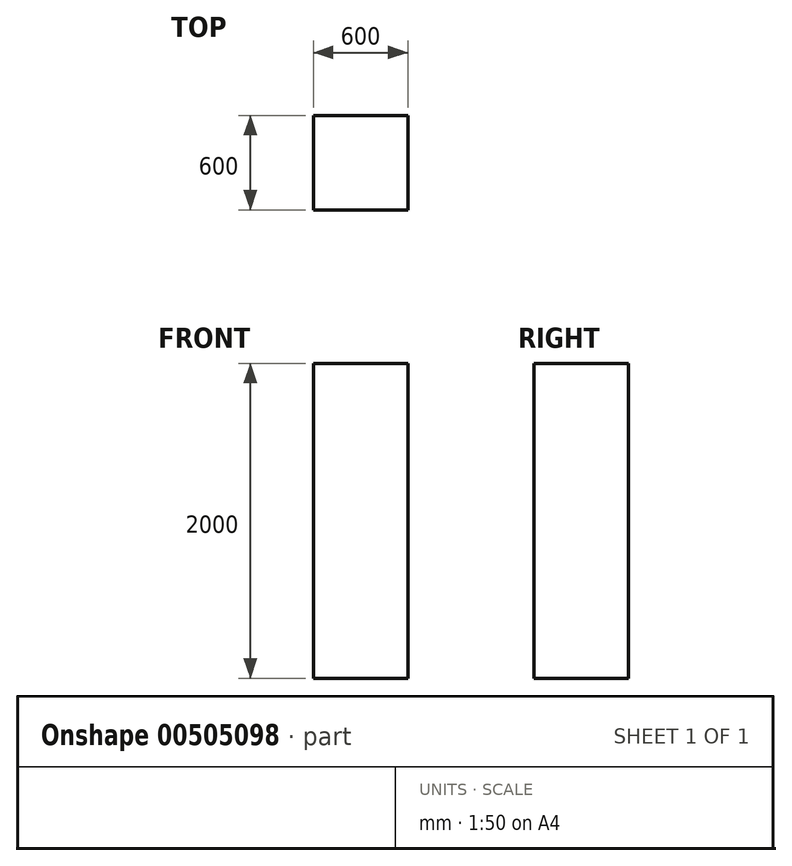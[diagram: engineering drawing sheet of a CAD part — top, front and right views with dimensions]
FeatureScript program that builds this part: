
annotation { "Feature Type Name" : "Feature", "Feature Type Description" : "" }
export const myFeature = defineFeature(function(context is Context, id is Id, definition is map)
    precondition{}
    {
        {
            var Q0;
            Q0=qCreatedBy(makeId("Top.planeOp"),FACE);
            var sketch = newSketch(context, id + "F0", { "sketchPlane" : qUnion([Q0])});
            skLineSegment(sketch, "E0.bottom", {"start": v(-330.23, 377) * mm, "end": v(269.77, 377) * mm});
            skLineSegment(sketch, "E0.top", {"start": v(-330.23, -223) * mm, "end": v(269.77, -223) * mm});
            skLineSegment(sketch, "E0.left", {"start": v(-330.23, 377) * mm, "end": v(-330.23, -223) * mm});
            skLineSegment(sketch, "E0.right", {"start": v(269.77, 377) * mm, "end": v(269.77, -223) * mm});
            skSolve(sketch);
        }
        {
            var Q0;
            Q0 = qSketchRegion(id + "F0", true);
            extrude(context, id + "F1", {"entities" : qUnion([Q0]), "depth" : 2000 * mm});
        }
    });
